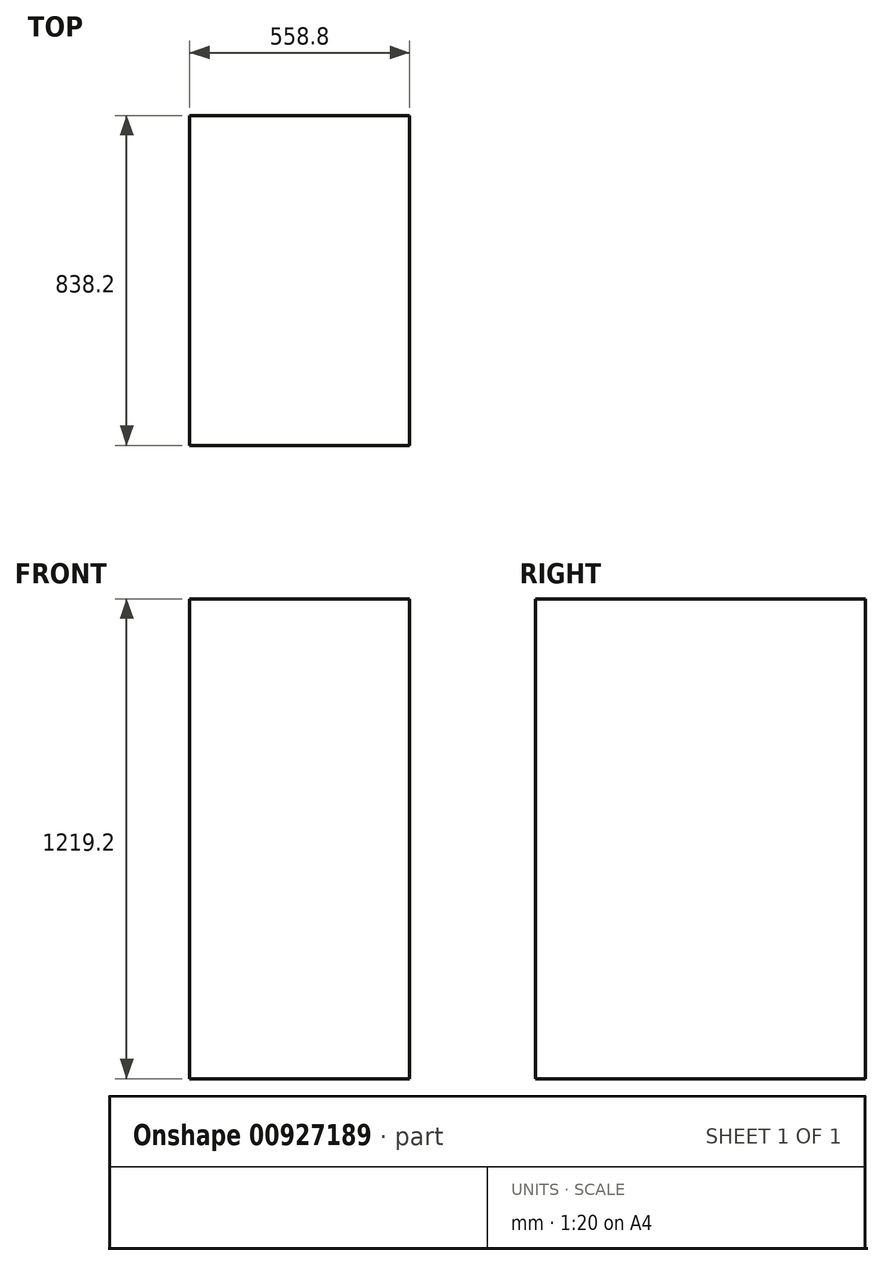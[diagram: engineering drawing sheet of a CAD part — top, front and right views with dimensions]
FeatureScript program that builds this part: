
annotation { "Feature Type Name" : "Feature", "Feature Type Description" : "" }
export const myFeature = defineFeature(function(context is Context, id is Id, definition is map)
    precondition{}
    {
        {
            var Q0;
            Q0=qCreatedBy(makeId("Top.planeOp"),FACE);
            var sketch = newSketch(context, id + "F0", { "sketchPlane" : qUnion([Q0])});
            skLineSegment(sketch, "E0.bottom", {"start": v(279.4, 419.1) * mm, "end": v(-279.4, 419.1) * mm});
            skLineSegment(sketch, "E0.top", {"start": v(279.4, -419.1) * mm, "end": v(-279.4, -419.1) * mm});
            skLineSegment(sketch, "E0.left", {"start": v(279.4, 419.1) * mm, "end": v(279.4, -419.1) * mm});
            skLineSegment(sketch, "E0.right", {"start": v(-279.4, 419.1) * mm, "end": v(-279.4, -419.1) * mm});
            skPoint(sketch, "E0.middle", {"position": v(0, 0) * mm});
            skSolve(sketch);
        }
        {
            var Q0;
            Q0 = qSketchRegion(id + "F0", true);
            extrude(context, id + "F1", {"entities" : qUnion([Q0]), "depth" : 1219.2 * mm, "offsetDistance" : 25.4 * mm});
        }
    });
